# Revit family: Haworth_BuzziFrontDesk
name_source: partatom
category: Furniture
revit_build: Autodesk Revit 2018 (Build: 20170223_1515(x64)
units: mm (PartAtom-declared; Revit-internal decimal feet)

## family parameters
Always vertical = Yes
Cut with Voids When Loaded = No
OmniClass Number = 23.40.70.14.64.21
OmniClass Title = Systems Furniture
Room Calculation Point = No
Shared = No
Work Plane-Based = No

## types (3) — shared parameters
Actual Depth = 3 45/128"
Actual Mounting Height = 4 1/8"
Actual Width = 70 223/256"
Assembly Code = E2020200
Custom Size = No
Manufacturer = Haworth
Max. Width = 70 223/256"
Min. Width = 39 95/256"
Model = HCBZ-FDS
Revision Number = 1
Rounded Corners = Yes
Size = Verify Final Dim. w/ Haworth
Squared Corners = No
Standard Widths = 39.37, 47.24, 55.12, 62.99, 70.87 in
URL = http://www.haworth.com
URL - Product = https://www.haworth.com
Void Length = 12"
Warranty = http://www.haworth.com
Width = 70 223/256"

## per-type parameters (varying)
| type | Actual Height | Description | High | Low | Medium |
| HCBZ-FDS1 - Low Screen | 35 55/128" | Haworth BuzziFrontDesk Low Screen | No | Yes | No |
| HCBZ-FDS2 - Medium Screen | 39 95/256" | Haworth BuzziFrontDesk Medium Screen | No | No | Yes |
| HCBZ-FDS3 - High Screen | 43 77/256" | Haworth BuzziFrontDesk High Screen | Yes | No | No |

## geometry (parser evidence)
native form markers: Sweep x3
no freeform markers — native parametric forms only
